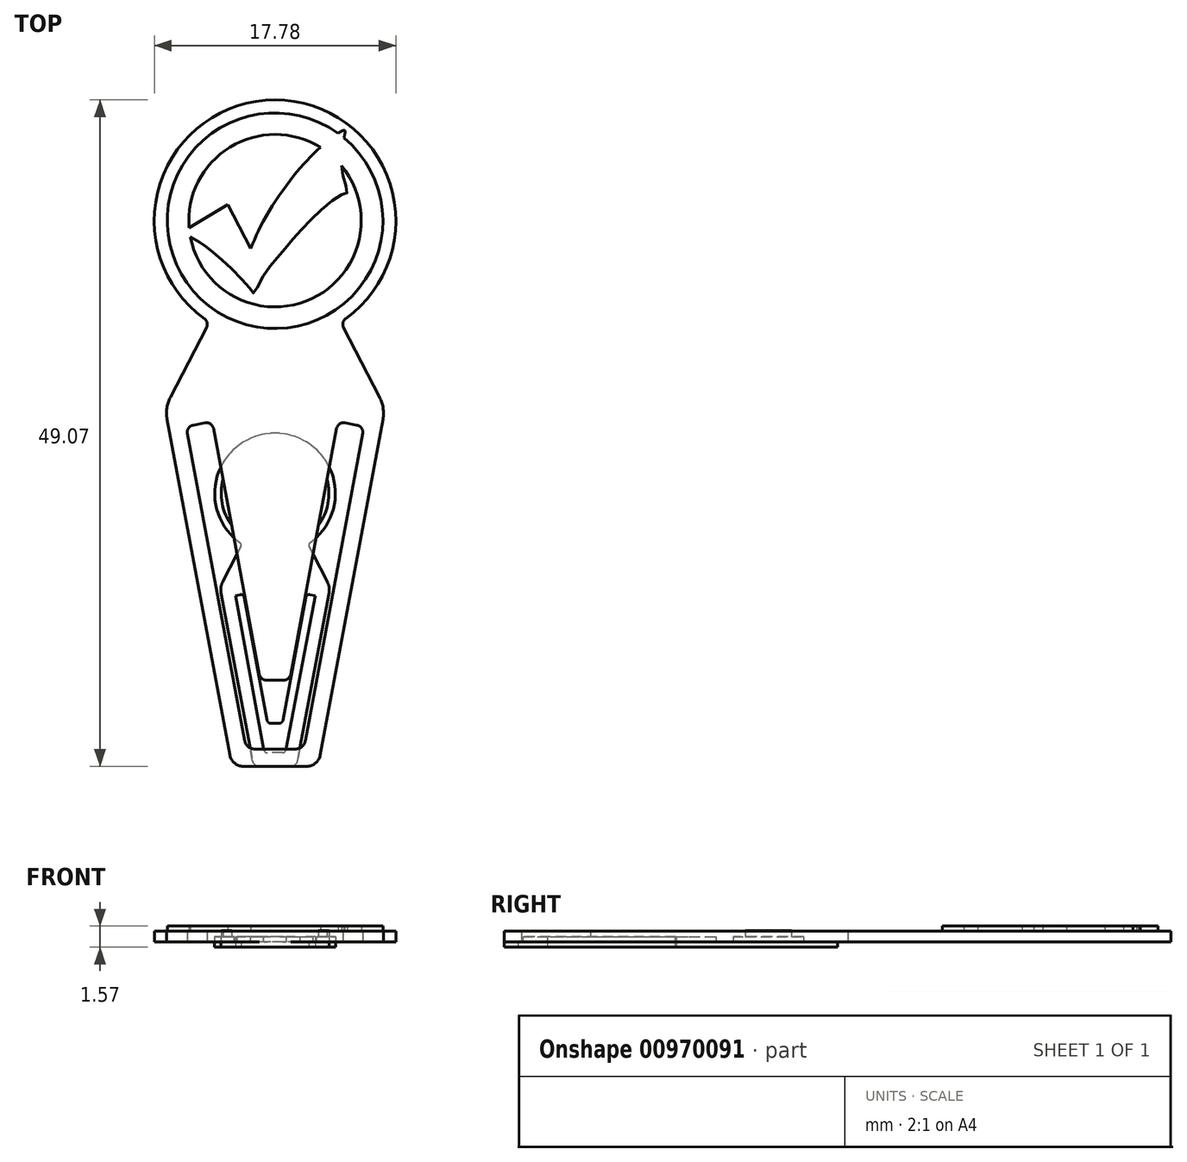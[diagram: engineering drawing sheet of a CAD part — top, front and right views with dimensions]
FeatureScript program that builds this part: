
annotation { "Feature Type Name" : "Feature", "Feature Type Description" : "" }
export const myFeature = defineFeature(function(context is Context, id is Id, definition is map)
    precondition{}
    {
        {
            var Q0;
            Q0=qCreatedBy(makeId("Top.planeOp"),FACE);
            var sketch = newSketch(context, id + "F0", { "sketchPlane" : qUnion([Q0])});
            skLineSegment(sketch, "E0", {"start": v(0, 0) * mm, "end": v(-2.33, 0) * mm});
            skLineSegment(sketch, "E1", {"start": v(-3.33, 0.83) * mm, "end": v(-7.94, 25.55) * mm});
            skLineSegment(sketch, "E2", {"start": v(-7.7, 27.18) * mm, "end": v(-5.05, 32.32) * mm});
            skLineSegment(sketch, "E3", {"start": v(0, 31.65) * mm, "end": v(0, 0) * mm});
            skLineSegment(sketch, "E4.MirrorCS", {"start": v(0, 0) * mm, "end": v(2.33, 0) * mm});
            skLineSegment(sketch, "E5.MirrorCS", {"start": v(3.33, 0.83) * mm, "end": v(7.94, 25.55) * mm});
            skLineSegment(sketch, "E6.MirrorCS", {"start": v(7.7, 27.18) * mm, "end": v(5.05, 32.32) * mm});
            skArc(sketch, "E7", {"start": v(5.2, 32.97) * mm, "mid": v(0, 49.07) * mm, "end": v(-5.2, 32.97) * mm});
            skPoint(sketch, "E8.visualSharp", {"position": v(-4.84, 32.72) * mm});
            skArc(sketch, "E8.filletArc", {"start": v(-5.05, 32.32) * mm, "mid": v(-5, 32.67) * mm, "end": v(-5.2, 32.97) * mm});
            skPoint(sketch, "E9.visualSharp", {"position": v(4.84, 32.72) * mm});
            skArc(sketch, "E9.filletArc", {"start": v(5.2, 32.97) * mm, "mid": v(5, 32.67) * mm, "end": v(5.05, 32.32) * mm});
            skPoint(sketch, "E10.visualSharp", {"position": v(-8.1, 26.4) * mm});
            skArc(sketch, "E10.filletArc", {"start": v(-7.7, 27.18) * mm, "mid": v(-7.96, 26.39) * mm, "end": v(-7.94, 25.55) * mm});
            skPoint(sketch, "E11.visualSharp", {"position": v(8.1, 26.4) * mm});
            skArc(sketch, "E11.filletArc", {"start": v(7.94, 25.55) * mm, "mid": v(7.96, 26.39) * mm, "end": v(7.7, 27.18) * mm});
            skLineSegment(sketch, "E12.0", {"start": v(-2.24, 1.9) * mm, "end": v(-6.46, 24.52) * mm});
            skLineSegment(sketch, "E13.0", {"start": v(-1.15, 6.76) * mm, "end": v(-4.53, 24.88) * mm});
            skLineSegment(sketch, "E14.0", {"start": v(2.24, 1.9) * mm, "end": v(6.46, 24.52) * mm});
            skLineSegment(sketch, "E15.0", {"start": v(1.15, 6.76) * mm, "end": v(4.53, 24.88) * mm});
            skLineSegment(sketch, "E16.0", {"start": v(1.49, 1.27) * mm, "end": v(-1.49, 1.27) * mm});
            skLineSegment(sketch, "E17.0", {"start": v(0.65, 6.35) * mm, "end": v(-0.65, 6.35) * mm});
            skLineSegment(sketch, "E18.filletArc", {"start": v(1.07, 6.35) * mm, "end": v(1.07, 6.35) * mm});
            skLineSegment(sketch, "E19.filletArc", {"start": v(-1.07, 6.35) * mm, "end": v(-1.07, 6.35) * mm});
            skLineSegment(sketch, "E20.filletArc", {"start": v(-2.12, 1.27) * mm, "end": v(-2.12, 1.27) * mm});
            skLineSegment(sketch, "E21", {"start": v(-6.05, 25.12) * mm, "end": v(-5.12, 25.29) * mm});
            skArc(sketch, "E22.filletArc", {"start": v(-6.05, 25.12) * mm, "mid": v(-6.38, 24.9) * mm, "end": v(-6.46, 24.52) * mm});
            skArc(sketch, "E23.filletArc", {"start": v(-4.53, 24.88) * mm, "mid": v(-4.74, 25.2) * mm, "end": v(-5.12, 25.29) * mm});
            skArc(sketch, "E24.MirrorCS", {"start": v(4.53, 24.88) * mm, "mid": v(4.74, 25.2) * mm, "end": v(5.12, 25.29) * mm});
            skArc(sketch, "E25.MirrorCS", {"start": v(6.05, 25.12) * mm, "mid": v(6.38, 24.9) * mm, "end": v(6.46, 24.52) * mm});
            skLineSegment(sketch, "E26.MirrorCS", {"start": v(6.05, 25.12) * mm, "end": v(5.12, 25.29) * mm});
            skArc(sketch, "E27.filletArc", {"start": v(-2.24, 1.9) * mm, "mid": v(-1.97, 1.45) * mm, "end": v(-1.49, 1.27) * mm});
            skPoint(sketch, "E28.visualSharp", {"position": v(-3.18, 0) * mm});
            skArc(sketch, "E28.filletArc", {"start": v(-3.33, 0.83) * mm, "mid": v(-2.98, 0.23) * mm, "end": v(-2.33, 0) * mm});
            skPoint(sketch, "E29.visualSharp", {"position": v(3.18, 0) * mm});
            skArc(sketch, "E29.filletArc", {"start": v(2.33, 0) * mm, "mid": v(2.98, 0.23) * mm, "end": v(3.33, 0.83) * mm});
            skPoint(sketch, "E30.visualSharp", {"position": v(2.12, 1.27) * mm});
            skArc(sketch, "E30.filletArc", {"start": v(1.49, 1.27) * mm, "mid": v(1.97, 1.45) * mm, "end": v(2.24, 1.9) * mm});
            skArc(sketch, "E31.filletArc", {"start": v(0.65, 6.35) * mm, "mid": v(0.98, 6.47) * mm, "end": v(1.15, 6.76) * mm});
            skArc(sketch, "E32.filletArc", {"start": v(-1.15, 6.76) * mm, "mid": v(-0.98, 6.47) * mm, "end": v(-0.65, 6.35) * mm});
            skSolve(sketch);
        }
        {
            var Q0;
            Q0 = qSketchRegion(id + "F0", true);
            extrude(context, id + "F1", {"entities" : qUnion([Q0]), "depth" : 0.8 * mm, "offsetDistance" : 25.4 * mm});
        }
        {
            var Q0;
            Q0=makeQuery(id+"F1.opExtrude","CAP_FACE",FACE,{"disambiguationData":[OSD([sQuery(id+"F0.wireOp",EDGE,"E0"),sQuery(id+"F0.wireOp",EDGE,"E1"),sQuery(id+"F0.wireOp",EDGE,"E2"),sQuery(id+"F0.wireOp",EDGE,"E4.MirrorCS"),sQuery(id+"F0.wireOp",EDGE,"E5.MirrorCS"),sQuery(id+"F0.wireOp",EDGE,"E6.MirrorCS"),sQuery(id+"F0.wireOp",EDGE,"E7"),sQuery(id+"F0.wireOp",EDGE,"E8.filletArc"),sQuery(id+"F0.wireOp",EDGE,"E9.filletArc"),sQuery(id+"F0.wireOp",EDGE,"E10.filletArc"),sQuery(id+"F0.wireOp",EDGE,"E11.filletArc"),sQuery(id+"F0.wireOp",EDGE,"E12.0"),sQuery(id+"F0.wireOp",EDGE,"E13.0"),sQuery(id+"F0.wireOp",EDGE,"E14.0"),sQuery(id+"F0.wireOp",EDGE,"E15.0"),sQuery(id+"F0.wireOp",EDGE,"E16.0"),sQuery(id+"F0.wireOp",EDGE,"E17.0"),sQuery(id+"F0.wireOp",EDGE,"E21"),sQuery(id+"F0.wireOp",EDGE,"E22.filletArc"),sQuery(id+"F0.wireOp",EDGE,"E23.filletArc"),sQuery(id+"F0.wireOp",EDGE,"E24.MirrorCS"),sQuery(id+"F0.wireOp",EDGE,"E25.MirrorCS"),sQuery(id+"F0.wireOp",EDGE,"E26.MirrorCS"),sQuery(id+"F0.wireOp",EDGE,"E27.filletArc"),sQuery(id+"F0.wireOp",EDGE,"E28.filletArc"),sQuery(id+"F0.wireOp",EDGE,"E29.filletArc"),sQuery(id+"F0.wireOp",EDGE,"E30.filletArc"),sQuery(id+"F0.wireOp",EDGE,"E31.filletArc"),sQuery(id+"F0.wireOp",EDGE,"E32.filletArc")])],"isStart":false});
            var sketch = newSketch(context, id + "F2", { "sketchPlane" : qUnion([Q0])});
            skLineSegment(sketch, "E33", {"start": v(-3.49, 41.38) * mm, "end": v(-1.8, 38.13) * mm});
            skLineSegment(sketch, "E34", {"start": v(-6.87, 39.3) * mm, "end": v(-3.49, 41.38) * mm});
            skFitSpline(sketch, "E35", {"points": [v(-1.8, 38.13) * mm, v(-0.95, 39.98) * mm, v(0.66, 42.54) * mm, v(2.23, 44.47) * mm, v(3.61, 45.82) * mm, v(5.12, 46.82) * mm, v(5.08, 46.3) * mm, v(4.9, 44.66) * mm, v(5.05, 43.31) * mm, v(5.3, 42.23) * mm, v(5.01, 42.14) * mm, v(3.37, 40.95) * mm, v(1.57, 39.12) * mm, v(0.28, 37.58) * mm, v(-0.9, 36.07) * mm, v(-1.57, 34.85) * mm, v(-1.8, 35.12) * mm, v(-3.36, 36.78) * mm, v(-4.74, 38.01) * mm, v(-5.54, 38.58) * mm, v(-6.87, 39.3) * mm], "startDerivative": vector(12.98, 31.03) * mm, "endDerivative": vector(-29.14, 15.12) * mm});
            skSolve(sketch);
        }
        {
            var Q0;
            Q0 = qSketchRegion(id + "F2", true);
            extrude(context, id + "F3", {"entities" : qUnion([Q0]), "operationType" : NewBodyOperationType.ADD, "depth" : 0.4 * mm, "offsetDistance" : 25.4 * mm});
        }
        {
            var Q0;
            Q0=makeQuery(id+"F1.opExtrude","CAP_FACE",FACE,{"disambiguationData":[OSD([sQuery(id+"F0.wireOp",EDGE,"E0"),sQuery(id+"F0.wireOp",EDGE,"E1"),sQuery(id+"F0.wireOp",EDGE,"E2"),sQuery(id+"F0.wireOp",EDGE,"E4.MirrorCS"),sQuery(id+"F0.wireOp",EDGE,"E5.MirrorCS"),sQuery(id+"F0.wireOp",EDGE,"E6.MirrorCS"),sQuery(id+"F0.wireOp",EDGE,"E7"),sQuery(id+"F0.wireOp",EDGE,"E8.filletArc"),sQuery(id+"F0.wireOp",EDGE,"E9.filletArc"),sQuery(id+"F0.wireOp",EDGE,"E10.filletArc"),sQuery(id+"F0.wireOp",EDGE,"E11.filletArc"),sQuery(id+"F0.wireOp",EDGE,"E12.0"),sQuery(id+"F0.wireOp",EDGE,"E13.0"),sQuery(id+"F0.wireOp",EDGE,"E14.0"),sQuery(id+"F0.wireOp",EDGE,"E15.0"),sQuery(id+"F0.wireOp",EDGE,"E16.0"),sQuery(id+"F0.wireOp",EDGE,"E17.0"),sQuery(id+"F0.wireOp",EDGE,"E21"),sQuery(id+"F0.wireOp",EDGE,"E22.filletArc"),sQuery(id+"F0.wireOp",EDGE,"E23.filletArc"),sQuery(id+"F0.wireOp",EDGE,"E24.MirrorCS"),sQuery(id+"F0.wireOp",EDGE,"E25.MirrorCS"),sQuery(id+"F0.wireOp",EDGE,"E26.MirrorCS"),sQuery(id+"F0.wireOp",EDGE,"E27.filletArc"),sQuery(id+"F0.wireOp",EDGE,"E28.filletArc"),sQuery(id+"F0.wireOp",EDGE,"E29.filletArc"),sQuery(id+"F0.wireOp",EDGE,"E30.filletArc"),sQuery(id+"F0.wireOp",EDGE,"E31.filletArc"),sQuery(id+"F0.wireOp",EDGE,"E32.filletArc")])],"isStart":false});
            var sketch = newSketch(context, id + "F4", { "sketchPlane" : qUnion([Q0])});
            skCircle(sketch, "E36", {"center": v(0, 40.18) * mm, "radius": 6.35 * mm});
            skCircle(sketch, "E37.0", {"center": v(0, 40.18) * mm, "radius": 7.94 * mm});
            skSolve(sketch);
        }
        {
            var Q0;
            Q0 = qSketchRegion(id + "F4", true);
            extrude(context, id + "F5", {"entities" : qUnion([Q0]), "operationType" : NewBodyOperationType.ADD, "depth" : 0.4 * mm, "offsetDistance" : 25.4 * mm});
        }
        {
            var Q0;
            Q0=makeQuery(id+"F1.opExtrude","SWEPT_BODY",BODY,{"disambiguationData":[OSD([sQuery(id+"F0.wireOp",EDGE,"E0"),sQuery(id+"F0.wireOp",EDGE,"E1"),sQuery(id+"F0.wireOp",EDGE,"E2"),sQuery(id+"F0.wireOp",EDGE,"E4.MirrorCS"),sQuery(id+"F0.wireOp",EDGE,"E5.MirrorCS"),sQuery(id+"F0.wireOp",EDGE,"E6.MirrorCS"),sQuery(id+"F0.wireOp",EDGE,"E7"),sQuery(id+"F0.wireOp",EDGE,"E8.filletArc"),sQuery(id+"F0.wireOp",EDGE,"E9.filletArc"),sQuery(id+"F0.wireOp",EDGE,"E10.filletArc"),sQuery(id+"F0.wireOp",EDGE,"E11.filletArc"),sQuery(id+"F0.wireOp",EDGE,"E12.0"),sQuery(id+"F0.wireOp",EDGE,"E13.0"),sQuery(id+"F0.wireOp",EDGE,"E14.0"),sQuery(id+"F0.wireOp",EDGE,"E15.0"),sQuery(id+"F0.wireOp",EDGE,"E16.0"),sQuery(id+"F0.wireOp",EDGE,"E17.0"),sQuery(id+"F0.wireOp",EDGE,"E21"),sQuery(id+"F0.wireOp",EDGE,"E22.filletArc"),sQuery(id+"F0.wireOp",EDGE,"E23.filletArc"),sQuery(id+"F0.wireOp",EDGE,"E24.MirrorCS"),sQuery(id+"F0.wireOp",EDGE,"E25.MirrorCS"),sQuery(id+"F0.wireOp",EDGE,"E26.MirrorCS"),sQuery(id+"F0.wireOp",EDGE,"E27.filletArc"),sQuery(id+"F0.wireOp",EDGE,"E28.filletArc"),sQuery(id+"F0.wireOp",EDGE,"E29.filletArc"),sQuery(id+"F0.wireOp",EDGE,"E30.filletArc"),sQuery(id+"F0.wireOp",EDGE,"E31.filletArc"),sQuery(id+"F0.wireOp",EDGE,"E32.filletArc")])]});
            var Q1;
            Q1=qCreatedBy(makeId("Origin.pointOp"),VERTEX);
            transform(context, id + "F6", {"entities" : qUnion([Q0]), "transformType" : TransformType.SCALE_UNIFORMLY, "scale" : .5, "scalePoint" : qUnion([Q1]), "makeCopy" : true});
        }
        {
            var Q0;
            Q0=makeQuery(id+"F6.opPattern","COPY",FACE,{"derivedFrom":makeQuery(id+"F1.opExtrude","CAP_FACE",FACE,{"disambiguationData":[OSD([sQuery(id+"F0.wireOp",EDGE,"E0"),sQuery(id+"F0.wireOp",EDGE,"E1"),sQuery(id+"F0.wireOp",EDGE,"E2"),sQuery(id+"F0.wireOp",EDGE,"E4.MirrorCS"),sQuery(id+"F0.wireOp",EDGE,"E5.MirrorCS"),sQuery(id+"F0.wireOp",EDGE,"E6.MirrorCS"),sQuery(id+"F0.wireOp",EDGE,"E7"),sQuery(id+"F0.wireOp",EDGE,"E8.filletArc"),sQuery(id+"F0.wireOp",EDGE,"E9.filletArc"),sQuery(id+"F0.wireOp",EDGE,"E10.filletArc"),sQuery(id+"F0.wireOp",EDGE,"E11.filletArc"),sQuery(id+"F0.wireOp",EDGE,"E12.0"),sQuery(id+"F0.wireOp",EDGE,"E13.0"),sQuery(id+"F0.wireOp",EDGE,"E14.0"),sQuery(id+"F0.wireOp",EDGE,"E15.0"),sQuery(id+"F0.wireOp",EDGE,"E16.0"),sQuery(id+"F0.wireOp",EDGE,"E17.0"),sQuery(id+"F0.wireOp",EDGE,"E21"),sQuery(id+"F0.wireOp",EDGE,"E22.filletArc"),sQuery(id+"F0.wireOp",EDGE,"E23.filletArc"),sQuery(id+"F0.wireOp",EDGE,"E24.MirrorCS"),sQuery(id+"F0.wireOp",EDGE,"E25.MirrorCS"),sQuery(id+"F0.wireOp",EDGE,"E26.MirrorCS"),sQuery(id+"F0.wireOp",EDGE,"E27.filletArc"),sQuery(id+"F0.wireOp",EDGE,"E28.filletArc"),sQuery(id+"F0.wireOp",EDGE,"E29.filletArc"),sQuery(id+"F0.wireOp",EDGE,"E30.filletArc"),sQuery(id+"F0.wireOp",EDGE,"E31.filletArc"),sQuery(id+"F0.wireOp",EDGE,"E32.filletArc")])],"isStart":true}),"instanceName":"1"});
            extrude(context, id + "F7", {"entities" : qUnion([Q0]), "operationType" : NewBodyOperationType.ADD, "depth" : 0.38 * mm, "offsetDistance" : 25.4 * mm});
        }
        {
            var Q0;
            Q0=qCreatedBy(makeId("Top.planeOp"),FACE);
            var sketch = newSketch(context, id + "F8", { "sketchPlane" : qUnion([Q0])});
            skLineSegment(sketch, "E38", {"start": v(-2.93, 12.66) * mm, "end": v(-0.82, 1.2) * mm});
            skLineSegment(sketch, "E39", {"start": v(-0.57, 1) * mm, "end": v(0.55, 1) * mm});
            skLineSegment(sketch, "E40", {"start": v(0.8, 1.2) * mm, "end": v(2.98, 12.6) * mm});
            skLineSegment(sketch, "E41", {"start": v(2.98, 12.6) * mm, "end": v(3.35, 12.53) * mm});
            skLineSegment(sketch, "E42", {"start": v(3.35, 12.53) * mm, "end": v(1.07, 0.58) * mm});
            skLineSegment(sketch, "E43", {"start": v(1.07, 0.58) * mm, "end": v(-1.09, 0.58) * mm});
            skLineSegment(sketch, "E44", {"start": v(-1.09, 0.58) * mm, "end": v(-3.3, 12.6) * mm});
            skLineSegment(sketch, "E45", {"start": v(-3.3, 12.6) * mm, "end": v(-2.93, 12.66) * mm});
            skPoint(sketch, "E46.visualSharp", {"position": v(-0.78, 1) * mm});
            skArc(sketch, "E46.filletArc", {"start": v(-0.82, 1.2) * mm, "mid": v(-0.73, 1.06) * mm, "end": v(-0.57, 1) * mm});
            skPoint(sketch, "E47.visualSharp", {"position": v(0.76, 1) * mm});
            skArc(sketch, "E47.filletArc", {"start": v(0.55, 1) * mm, "mid": v(0.71, 1.06) * mm, "end": v(0.8, 1.2) * mm});
            skSolve(sketch);
        }
        {
            var Q0;
            Q0 = qSketchRegion(id + "F8", true);
            var Q1;
            {var subQ0=sQuery(id+"F0.wireOp",EDGE,"E26.MirrorCS");var subQ1=sQuery(id+"F0.wireOp",EDGE,"E25.MirrorCS");var subQ2=sQuery(id+"F0.wireOp",EDGE,"E24.MirrorCS");var subQ3=sQuery(id+"F0.wireOp",EDGE,"E23.filletArc");var subQ4=sQuery(id+"F0.wireOp",EDGE,"E22.filletArc");var subQ5=sQuery(id+"F0.wireOp",EDGE,"E21");var subQ6=sQuery(id+"F0.wireOp",EDGE,"E17.0");var subQ7=sQuery(id+"F0.wireOp",EDGE,"E16.0");var subQ8=sQuery(id+"F0.wireOp",EDGE,"E15.0");var subQ9=sQuery(id+"F0.wireOp",EDGE,"E14.0");var subQ10=sQuery(id+"F0.wireOp",EDGE,"E13.0");var subQ11=sQuery(id+"F0.wireOp",EDGE,"E12.0");var subQ12=sQuery(id+"F0.wireOp",EDGE,"E5.MirrorCS");var subQ13=sQuery(id+"F0.wireOp",EDGE,"E2");var subQ14=sQuery(id+"F0.wireOp",EDGE,"E1");var subQ15=sQuery(id+"F0.wireOp",EDGE,"E4.MirrorCS");var subQ16=sQuery(id+"F0.wireOp",EDGE,"E0");var subQ17=sQuery(id+"F0.wireOp",EDGE,"E6.MirrorCS");var subQ18=sQuery(id+"F0.wireOp",EDGE,"E7");var subQ19=sQuery(id+"F0.wireOp",EDGE,"E8.filletArc");var subQ20=sQuery(id+"F0.wireOp",EDGE,"E9.filletArc");var subQ21=sQuery(id+"F0.wireOp",EDGE,"E10.filletArc");var subQ22=sQuery(id+"F0.wireOp",EDGE,"E11.filletArc");var subQ23=sQuery(id+"F0.wireOp",EDGE,"E27.filletArc");var subQ24=sQuery(id+"F0.wireOp",EDGE,"E28.filletArc");var subQ25=sQuery(id+"F0.wireOp",EDGE,"E29.filletArc");var subQ26=sQuery(id+"F0.wireOp",EDGE,"E30.filletArc");var subQ27=sQuery(id+"F0.wireOp",EDGE,"E31.filletArc");var subQ28=sQuery(id+"F0.wireOp",EDGE,"E32.filletArc");Q1=makeQuery(id+"F6.opPattern","COPY",FACE,{"derivedFrom":makeQuery(id+"F5.boolean.opBoolean","SPLIT",FACE,{"disambiguationData":[TD([makeQuery(id+"F1.opExtrude","SWEPT_FACE",FACE,{"disambiguationData":[OSD([subQ16,subQ15])]}),makeQuery(id+"F1.opExtrude","SWEPT_FACE",FACE,{"disambiguationData":[OSD([subQ14])]}),makeQuery(id+"F1.opExtrude","SWEPT_FACE",FACE,{"disambiguationData":[OSD([subQ13])]}),makeQuery(id+"F1.opExtrude","SWEPT_FACE",FACE,{"disambiguationData":[OSD([subQ12])]}),makeQuery(id+"F1.opExtrude","SWEPT_FACE",FACE,{"disambiguationData":[OSD([subQ17])]}),makeQuery(id+"F1.opExtrude","SWEPT_FACE",FACE,{"disambiguationData":[OSD([subQ18])]}),makeQuery(id+"F1.opExtrude","SWEPT_FACE",FACE,{"disambiguationData":[OSD([subQ19])]}),makeQuery(id+"F1.opExtrude","SWEPT_FACE",FACE,{"disambiguationData":[OSD([subQ20])]}),makeQuery(id+"F1.opExtrude","SWEPT_FACE",FACE,{"disambiguationData":[OSD([subQ21])]}),makeQuery(id+"F1.opExtrude","SWEPT_FACE",FACE,{"disambiguationData":[OSD([subQ22])]}),makeQuery(id+"F1.opExtrude","SWEPT_FACE",FACE,{"disambiguationData":[OSD([subQ11])]}),makeQuery(id+"F1.opExtrude","SWEPT_FACE",FACE,{"disambiguationData":[OSD([subQ10])]}),makeQuery(id+"F1.opExtrude","SWEPT_FACE",FACE,{"disambiguationData":[OSD([subQ9])]}),makeQuery(id+"F1.opExtrude","SWEPT_FACE",FACE,{"disambiguationData":[OSD([subQ8])]}),makeQuery(id+"F1.opExtrude","SWEPT_FACE",FACE,{"disambiguationData":[OSD([subQ7])]}),makeQuery(id+"F1.opExtrude","SWEPT_FACE",FACE,{"disambiguationData":[OSD([subQ6])]}),makeQuery(id+"F1.opExtrude","SWEPT_FACE",FACE,{"disambiguationData":[OSD([subQ5])]}),makeQuery(id+"F1.opExtrude","SWEPT_FACE",FACE,{"disambiguationData":[OSD([subQ4])]}),makeQuery(id+"F1.opExtrude","SWEPT_FACE",FACE,{"disambiguationData":[OSD([subQ3])]}),makeQuery(id+"F1.opExtrude","SWEPT_FACE",FACE,{"disambiguationData":[OSD([subQ2])]}),makeQuery(id+"F1.opExtrude","SWEPT_FACE",FACE,{"disambiguationData":[OSD([subQ1])]}),makeQuery(id+"F1.opExtrude","SWEPT_FACE",FACE,{"disambiguationData":[OSD([subQ0])]}),makeQuery(id+"F1.opExtrude","SWEPT_FACE",FACE,{"disambiguationData":[OSD([subQ23])]}),makeQuery(id+"F1.opExtrude","SWEPT_FACE",FACE,{"disambiguationData":[OSD([subQ24])]}),makeQuery(id+"F1.opExtrude","SWEPT_FACE",FACE,{"disambiguationData":[OSD([subQ25])]}),makeQuery(id+"F1.opExtrude","SWEPT_FACE",FACE,{"disambiguationData":[OSD([subQ26])]}),makeQuery(id+"F1.opExtrude","SWEPT_FACE",FACE,{"disambiguationData":[OSD([subQ27])]}),makeQuery(id+"F1.opExtrude","SWEPT_FACE",FACE,{"disambiguationData":[OSD([subQ28])]}),makeQuery(id+"F3.opExtrude","SWEPT_FACE",FACE,{"disambiguationData":[OSD([sQuery(id+"F2.wireOp",EDGE,"E35")])]}),makeQuery(id+"F5.opExtrude","SWEPT_FACE",FACE,{"disambiguationData":[OSD([sQuery(id+"F4.wireOp",EDGE,"E37.0")])]})])],"derivedFrom":makeQuery(id+"F1.opExtrude","CAP_FACE",FACE,{"disambiguationData":[OSD([subQ16,subQ14,subQ13,subQ15,subQ12,subQ17,subQ18,subQ19,subQ20,subQ21,subQ22,subQ11,subQ10,subQ9,subQ8,subQ7,subQ6,subQ5,subQ4,subQ3,subQ2,subQ1,subQ0,subQ23,subQ24,subQ25,subQ26,subQ27,subQ28])],"isStart":false})}),"instanceName":"1"});}
            var Q2;
            Q2=makeQuery(id+"F7.opExtrude","CAP_FACE",FACE,{"disambiguationData":[OSD([sQuery(id+"F0.wireOp",EDGE,"E0"),sQuery(id+"F0.wireOp",EDGE,"E1"),sQuery(id+"F0.wireOp",EDGE,"E2"),sQuery(id+"F0.wireOp",EDGE,"E4.MirrorCS"),sQuery(id+"F0.wireOp",EDGE,"E5.MirrorCS"),sQuery(id+"F0.wireOp",EDGE,"E6.MirrorCS"),sQuery(id+"F0.wireOp",EDGE,"E7"),sQuery(id+"F0.wireOp",EDGE,"E8.filletArc"),sQuery(id+"F0.wireOp",EDGE,"E9.filletArc"),sQuery(id+"F0.wireOp",EDGE,"E10.filletArc"),sQuery(id+"F0.wireOp",EDGE,"E11.filletArc"),sQuery(id+"F0.wireOp",EDGE,"E12.0"),sQuery(id+"F0.wireOp",EDGE,"E13.0"),sQuery(id+"F0.wireOp",EDGE,"E14.0"),sQuery(id+"F0.wireOp",EDGE,"E15.0"),sQuery(id+"F0.wireOp",EDGE,"E16.0"),sQuery(id+"F0.wireOp",EDGE,"E17.0"),sQuery(id+"F0.wireOp",EDGE,"E21"),sQuery(id+"F0.wireOp",EDGE,"E22.filletArc"),sQuery(id+"F0.wireOp",EDGE,"E23.filletArc"),sQuery(id+"F0.wireOp",EDGE,"E24.MirrorCS"),sQuery(id+"F0.wireOp",EDGE,"E25.MirrorCS"),sQuery(id+"F0.wireOp",EDGE,"E26.MirrorCS"),sQuery(id+"F0.wireOp",EDGE,"E27.filletArc"),sQuery(id+"F0.wireOp",EDGE,"E28.filletArc"),sQuery(id+"F0.wireOp",EDGE,"E29.filletArc"),sQuery(id+"F0.wireOp",EDGE,"E30.filletArc"),sQuery(id+"F0.wireOp",EDGE,"E31.filletArc"),sQuery(id+"F0.wireOp",EDGE,"E32.filletArc")])],"isStart":false});
            extrude(context, id + "F9", {"entities" : qUnion([Q0]), "operationType" : NewBodyOperationType.ADD, "endBound" : BoundingType.UP_TO_SURFACE, "depth" : 25.4 * mm, "endBoundEntityFace" : qUnion([Q1]), "offsetDistance" : 25.4 * mm, "hasSecondDirection" : true, "secondDirectionBound" : SecondDirectionBoundingType.UP_TO_SURFACE, "secondDirectionOppositeDirection" : true, "secondDirectionDepth" : 25.4 * mm, "secondDirectionBoundEntityFace" : qUnion([Q2])});
        }
        {
            var Q0;
            Q0=makeQuery(id+"F6.opPattern","COPY",FACE,{"derivedFrom":makeQuery(id+"F5.boolean.opBoolean","MERGE",FACE,{"derivedFrom":[makeQuery(id+"F3.opExtrude","CAP_FACE",FACE,{"disambiguationData":[OSD([sQuery(id+"F2.wireOp",EDGE,"E33"),sQuery(id+"F2.wireOp",EDGE,"E34"),sQuery(id+"F2.wireOp",EDGE,"E35")])],"isStart":false}),makeQuery(id+"F5.opExtrude","CAP_FACE",FACE,{"disambiguationData":[OSD([sQuery(id+"F4.wireOp",EDGE,"E36"),sQuery(id+"F4.wireOp",EDGE,"E37.0")])],"isStart":false})]}),"instanceName":"1"});
            extrude(context, id + "F10", {"entities" : qUnion([Q0]), "operationType" : NewBodyOperationType.ADD, "depth" : 0.25 * mm, "offsetDistance" : 25.4 * mm});
        }
    });
